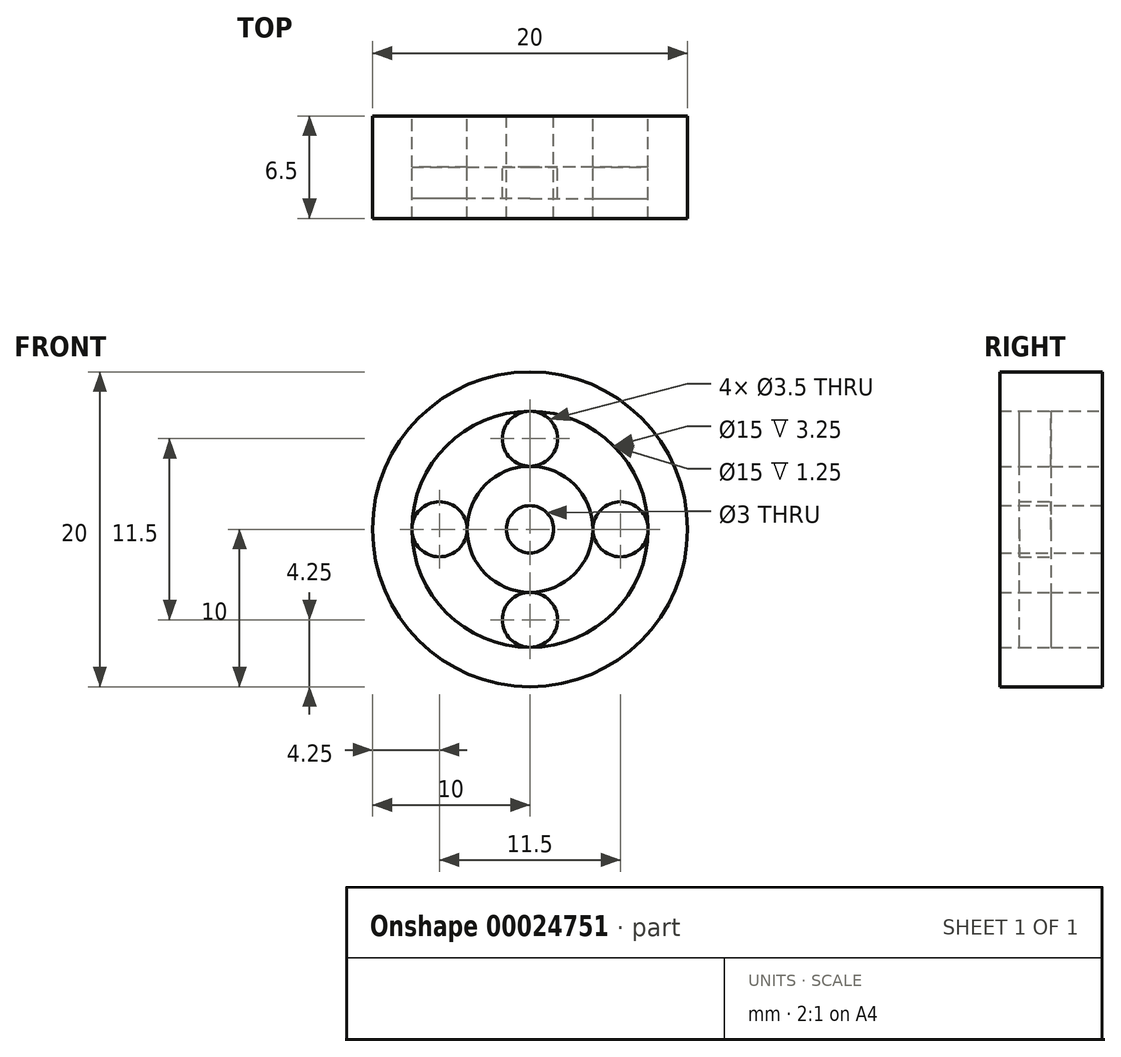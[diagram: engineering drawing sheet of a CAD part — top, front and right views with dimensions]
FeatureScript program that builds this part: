
annotation { "Feature Type Name" : "Feature", "Feature Type Description" : "" }
export const myFeature = defineFeature(function(context is Context, id is Id, definition is map)
    precondition{}
    {
        {
            var Q0;
            Q0=qCreatedBy(makeId("Front.planeOp"),FACE);
            var sketch = newSketch(context, id + "F0", { "sketchPlane" : qUnion([Q0])});
            skCircle(sketch, "E0", {"center": v(0, 0) * mm, "radius": 10 * mm});
            skCircle(sketch, "E1", {"center": v(0, 0) * mm, "radius": 7.5 * mm});
            skCircle(sketch, "E2", {"center": v(0, 0) * mm, "radius": 4 * mm});
            skCircle(sketch, "E3", {"center": v(0, 0) * mm, "radius": 1.5 * mm});
            skLineSegment(sketch, "E4", {"start": v(0, 4) * mm, "end": v(0, 7.5) * mm});
            skCircle(sketch, "E5", {"center": v(0, 5.75) * mm, "radius": 1.75 * mm});
            skCircle(sketch, "E6.1.0", {"center": v(-5.75, 0) * mm, "radius": 1.75 * mm});
            skCircle(sketch, "E6.2.0", {"center": v(0, -5.75) * mm, "radius": 1.75 * mm});
            skCircle(sketch, "E6.3.0", {"center": v(5.75, 0) * mm, "radius": 1.75 * mm});
            skSolve(sketch);
        }
        {
            var Q0;
            Q0=makeQuery(id+"F0.imprint","IMPRINT",FACE,{"disambiguationData":[TD([[makeQuery(id+"F0.imprint","IMPRINT",EDGE,{"derivedFrom":sQuery(id+"F0.wireOp",EDGE,"E0")}),1.0]])]});
            var Q1;
            Q1=makeQuery(id+"F0.imprint","IMPRINT",FACE,{"disambiguationData":[TD([[makeQuery(id+"F0.imprint","IMPRINT",EDGE,{"derivedFrom":sQuery(id+"F0.wireOp",EDGE,"E3")}),-1.0]])]});
            extrude(context, id + "F1", {"entities" : qUnion([Q0, Q1]), "endBound" : BoundingType.SYMMETRIC, "depth" : 6.5 * mm});
        }
        {
            var Q0;
            {var subQ3=sQuery(id+"F0.wireOp",EDGE,"E1");var subQ5=sQuery(id+"F0.wireOp",EDGE,"E6.1.0");var subQ7=makeQuery(id+"F0.imprint","INTERSECT",VERTEX,{"derivedFrom":[subQ3,subQ5]});Q0=makeQuery(id+"F0.imprint","IMPRINT",FACE,{"disambiguationData":[TD([[makeQuery(id+"F0.imprint","IMPRINT",EDGE,{"disambiguationData":[TD([[subQ7,-1.0]])],"derivedFrom":subQ3}),1.0]])]});}
            var Q1;
            {var subQ0=sQuery(id+"F0.wireOp",EDGE,"E6.1.0");var subQ3=sQuery(id+"F0.wireOp",EDGE,"E1");var subQ4=makeQuery(id+"F0.imprint","INTERSECT",VERTEX,{"derivedFrom":[subQ3,subQ0]});Q1=makeQuery(id+"F0.imprint","IMPRINT",FACE,{"disambiguationData":[TD([[makeQuery(id+"F0.imprint","IMPRINT",EDGE,{"disambiguationData":[TD([[subQ4,1.0]])],"derivedFrom":subQ0}),-1.0]])]});}
            var Q2;
            {var subQ0=sQuery(id+"F0.wireOp",EDGE,"E6.3.0");var subQ3=sQuery(id+"F0.wireOp",EDGE,"E1");var subQ4=makeQuery(id+"F0.imprint","INTERSECT",VERTEX,{"derivedFrom":[subQ3,subQ0]});Q2=makeQuery(id+"F0.imprint","IMPRINT",FACE,{"disambiguationData":[TD([[makeQuery(id+"F0.imprint","IMPRINT",EDGE,{"disambiguationData":[TD([[subQ4,-1.0]])],"derivedFrom":subQ0}),-1.0]])]});}
            var Q3;
            {var subQ0=sQuery(id+"F0.wireOp",EDGE,"E6.3.0");var subQ3=sQuery(id+"F0.wireOp",EDGE,"E1");var subQ4=makeQuery(id+"F0.imprint","INTERSECT",VERTEX,{"derivedFrom":[subQ3,subQ0]});Q3=makeQuery(id+"F0.imprint","IMPRINT",FACE,{"disambiguationData":[TD([[makeQuery(id+"F0.imprint","IMPRINT",EDGE,{"disambiguationData":[TD([[subQ4,1.0]])],"derivedFrom":subQ3}),1.0]])]});}
            extrude(context, id + "F2", {"entities" : qUnion([Q0, Q1, Q2, Q3]), "operationType" : NewBodyOperationType.ADD, "depth" : 2 * mm});
        }
    });
